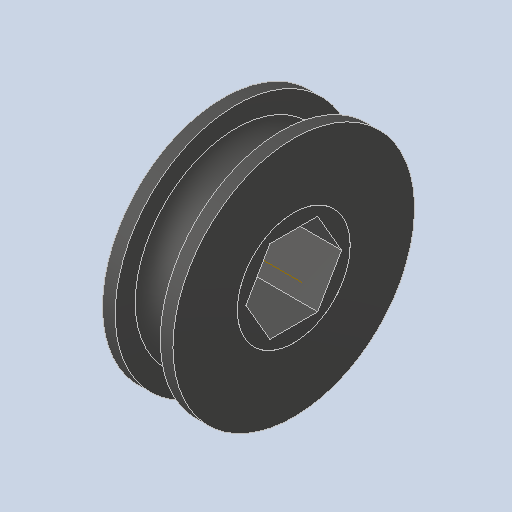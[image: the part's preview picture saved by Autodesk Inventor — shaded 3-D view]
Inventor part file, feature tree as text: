
AUTODESK INVENTOR PART (.ipt)
format: ipt  version: 2022.3 (Build 263350000, 350)  size: 178,176 bytes
history: native  units: in
note: dims shown in document units (in); Inventor stores cm internally (conversion verified against a paired STEP export)
features: thicken_offset x3, other x1, fillet x1
ambient origin geometry x8: Origin, YZ Plane, XZ Plane, XY Plane, X Axis, Y Axis, Z Axis, Center Point
bodies: Solid1 (feature_tree)
feature tree (5):
  thicken_offset  "Thicken1"
  thicken_offset  "Thicken2"
  thicken_offset  "Thicken3"
  other  "Work Axis1"
  fillet  "Fillet1"  Radius=0.015in
